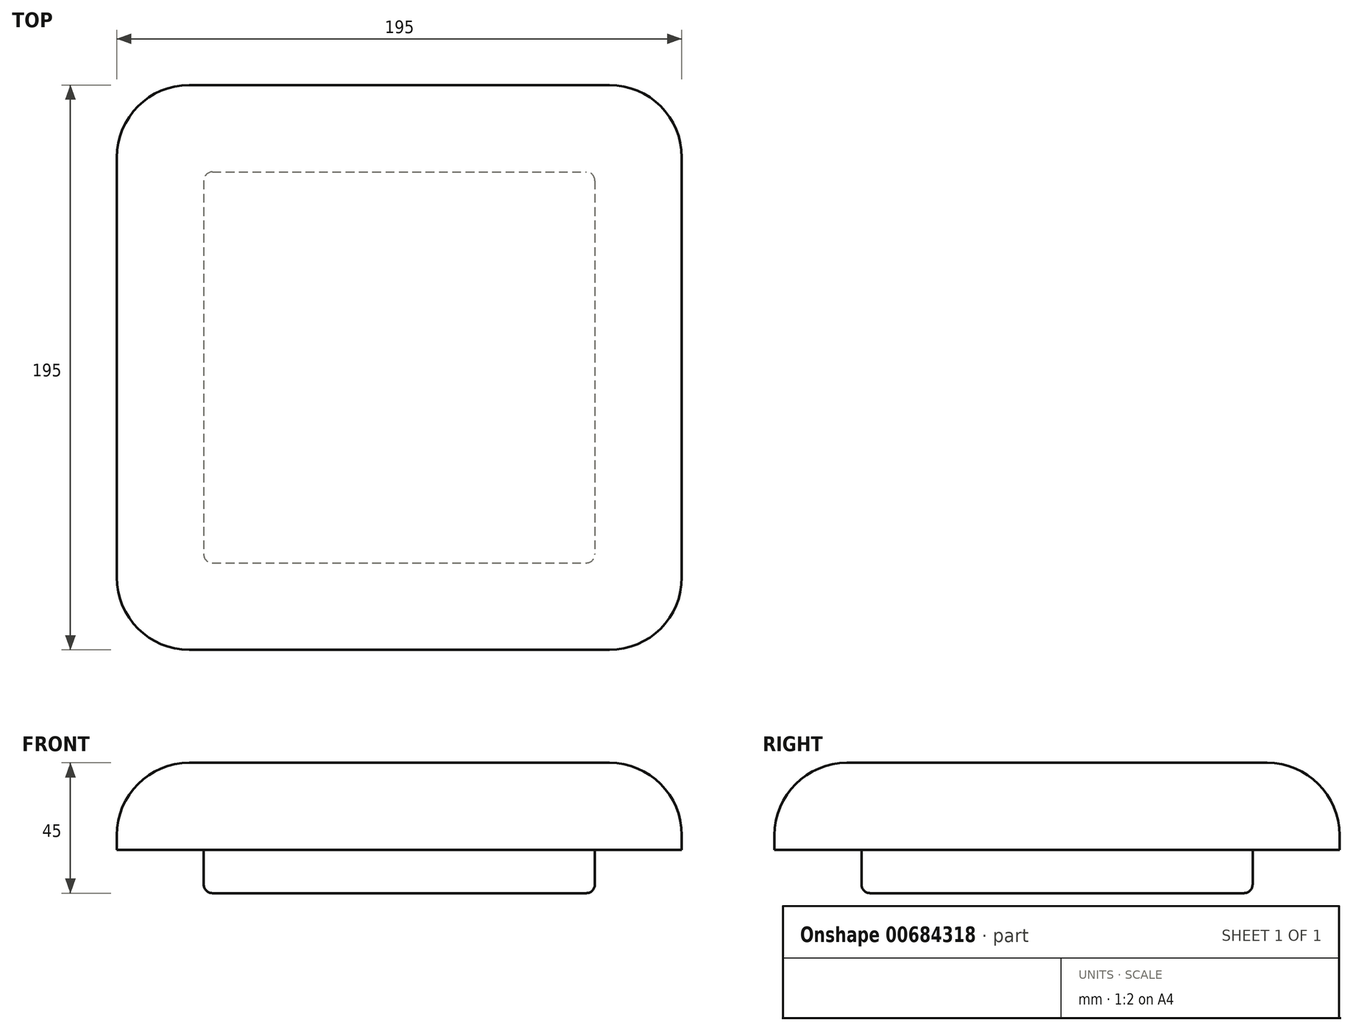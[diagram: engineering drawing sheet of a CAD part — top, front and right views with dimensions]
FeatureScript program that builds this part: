
annotation { "Feature Type Name" : "Feature", "Feature Type Description" : "" }
export const myFeature = defineFeature(function(context is Context, id is Id, definition is map)
    precondition{}
    {
        {
            var Q0;
            Q0=qCreatedBy(makeId("Top.planeOp"),FACE);
            var sketch = newSketch(context, id + "F0", { "sketchPlane" : qUnion([Q0])});
            skLineSegment(sketch, "E0.bottom", {"start": v(97.5, 97.5) * mm, "end": v(-97.5, 97.5) * mm});
            skLineSegment(sketch, "E0.top", {"start": v(97.5, -97.5) * mm, "end": v(-97.5, -97.5) * mm});
            skLineSegment(sketch, "E0.left", {"start": v(97.5, 97.5) * mm, "end": v(97.5, -97.5) * mm});
            skLineSegment(sketch, "E0.right", {"start": v(-97.5, 97.5) * mm, "end": v(-97.5, -97.5) * mm});
            skPoint(sketch, "E0.middle", {"position": v(0, 0) * mm});
            skSolve(sketch);
        }
        {
            var Q0;
            Q0=makeQuery(id+"F0.imprint","IMPRINT",FACE,{"disambiguationData":[TD([[makeQuery(id+"F0.imprint","IMPRINT",EDGE,{"derivedFrom":sQuery(id+"F0.wireOp",EDGE,"E0.bottom")}),1.0]])]});
            extrude(context, id + "F1", {"entities" : qUnion([Q0]), "depth" : 30 * mm, "offsetDistance" : 25 * mm});
        }
        {
            var Q0;
            Q0=makeQuery(id+"F1.opExtrude","CAP_FACE",FACE,{"disambiguationData":[OSD([sQuery(id+"F0.wireOp",EDGE,"E0.bottom"),sQuery(id+"F0.wireOp",EDGE,"E0.top"),sQuery(id+"F0.wireOp",EDGE,"E0.left"),sQuery(id+"F0.wireOp",EDGE,"E0.right")])],"isStart":false});
            var sketch = newSketch(context, id + "F2", { "sketchPlane" : qUnion([Q0])});
            skLineSegment(sketch, "E1.bottom", {"start": v(67.5, 67.5) * mm, "end": v(-67.5, 67.5) * mm});
            skLineSegment(sketch, "E1.top", {"start": v(67.5, -67.5) * mm, "end": v(-67.5, -67.5) * mm});
            skLineSegment(sketch, "E1.left", {"start": v(67.5, 67.5) * mm, "end": v(67.5, -67.5) * mm});
            skLineSegment(sketch, "E1.right", {"start": v(-67.5, 67.5) * mm, "end": v(-67.5, -67.5) * mm});
            skPoint(sketch, "E1.middle", {"position": v(0, 0) * mm});
            skSolve(sketch);
        }
        {
            var Q0;
            Q0=makeQuery(id+"F2.imprint","IMPRINT",FACE,{"disambiguationData":[TD([[makeQuery(id+"F2.imprint","IMPRINT",EDGE,{"derivedFrom":sQuery(id+"F2.wireOp",EDGE,"E1.bottom")}),1.0]])]});
            extrude(context, id + "F3", {"entities" : qUnion([Q0]), "operationType" : NewBodyOperationType.ADD, "depth" : 15 * mm, "offsetDistance" : 25 * mm});
        }
        {
            var Q0;
            Q0=makeQuery(id+"F3.opExtrude","CAP_FACE",FACE,{"disambiguationData":[OSD([sQuery(id+"F2.wireOp",EDGE,"E1.bottom"),sQuery(id+"F2.wireOp",EDGE,"E1.top"),sQuery(id+"F2.wireOp",EDGE,"E1.left"),sQuery(id+"F2.wireOp",EDGE,"E1.right")])],"isStart":false});
            var Q1;
            Q1=makeQuery(id+"F3.opExtrude","SWEPT_EDGE",EDGE,{"disambiguationData":[OSD([sQuery(id+"F2.wireOp",EDGE,"E1.top"),sQuery(id+"F2.wireOp",EDGE,"E1.left")])]});
            var Q2;
            Q2=makeQuery(id+"F3.opExtrude","SWEPT_EDGE",EDGE,{"disambiguationData":[OSD([sQuery(id+"F2.wireOp",EDGE,"E1.bottom"),sQuery(id+"F2.wireOp",EDGE,"E1.left")])]});
            var Q3;
            Q3=makeQuery(id+"F3.opExtrude","SWEPT_EDGE",EDGE,{"disambiguationData":[OSD([sQuery(id+"F2.wireOp",EDGE,"E1.top"),sQuery(id+"F2.wireOp",EDGE,"E1.right")])]});
            var Q4;
            Q4=makeQuery(id+"F3.opExtrude","SWEPT_EDGE",EDGE,{"disambiguationData":[OSD([sQuery(id+"F2.wireOp",EDGE,"E1.bottom"),sQuery(id+"F2.wireOp",EDGE,"E1.right")])]});
            fillet(context, id + "F4", {"entities" : qUnion([Q0, Q1, Q2, Q3, Q4]), "radius" : 3 * mm, "tangentPropagation" : true, "allowEdgeOverflow" : false});
        }
        {
            var Q0;
            Q0=makeQuery(id+"F1.opExtrude","CAP_FACE",FACE,{"disambiguationData":[OSD([sQuery(id+"F0.wireOp",EDGE,"E0.bottom"),sQuery(id+"F0.wireOp",EDGE,"E0.top"),sQuery(id+"F0.wireOp",EDGE,"E0.left"),sQuery(id+"F0.wireOp",EDGE,"E0.right")])],"isStart":true});
            var Q1;
            Q1=makeQuery(id+"F1.opExtrude","SWEPT_EDGE",EDGE,{"disambiguationData":[OSD([sQuery(id+"F0.wireOp",EDGE,"E0.bottom"),sQuery(id+"F0.wireOp",EDGE,"E0.left")])]});
            var Q2;
            Q2=makeQuery(id+"F1.opExtrude","SWEPT_EDGE",EDGE,{"disambiguationData":[OSD([sQuery(id+"F0.wireOp",EDGE,"E0.bottom"),sQuery(id+"F0.wireOp",EDGE,"E0.right")])]});
            var Q3;
            Q3=makeQuery(id+"F1.opExtrude","SWEPT_EDGE",EDGE,{"disambiguationData":[OSD([sQuery(id+"F0.wireOp",EDGE,"E0.top"),sQuery(id+"F0.wireOp",EDGE,"E0.right")])]});
            var Q4;
            Q4=makeQuery(id+"F1.opExtrude","SWEPT_EDGE",EDGE,{"disambiguationData":[OSD([sQuery(id+"F0.wireOp",EDGE,"E0.top"),sQuery(id+"F0.wireOp",EDGE,"E0.left")])]});
            fillet(context, id + "F5", {"entities" : qUnion([Q0, Q1, Q2, Q3, Q4]), "radius" : 25 * mm, "tangentPropagation" : true, "allowEdgeOverflow" : false});
        }
        {
            var Q0;
            Q0=makeQuery(id+"F1.opExtrude","SWEPT_BODY",BODY,{"disambiguationData":[OSD([sQuery(id+"F0.wireOp",EDGE,"E0.bottom"),sQuery(id+"F0.wireOp",EDGE,"E0.top"),sQuery(id+"F0.wireOp",EDGE,"E0.left"),sQuery(id+"F0.wireOp",EDGE,"E0.right")])]});
            var Q1;
            Q1=makeQuery(id+"F1.opExtrude","CAP_EDGE",EDGE,{"disambiguationData":[OSD([sQuery(id+"F0.wireOp",EDGE,"E0.left")])],"isStart":false});
            transform(context, id + "F6", {"entities" : qUnion([Q0]), "transformType" : TransformType.ROTATION, "transformAxis" : qUnion([Q1]), "angle" : 180 * degree, "makeCopy" : false});
        }
        {
            var Q0;
            Q0=makeQuery(id+"F1.opExtrude","SWEPT_BODY",BODY,{"disambiguationData":[OSD([sQuery(id+"F0.wireOp",EDGE,"E0.bottom"),sQuery(id+"F0.wireOp",EDGE,"E0.top"),sQuery(id+"F0.wireOp",EDGE,"E0.left"),sQuery(id+"F0.wireOp",EDGE,"E0.right")])]});
            transform(context, id + "F7", {"entities" : qUnion([Q0]), "transformType" : TransformType.TRANSLATION_3D, "dx" : -195 * mm, "dy" : 0 * mm, "dz" : 0 * mm, "makeCopy" : false});
        }
        {
            var Q0;
            Q0=makeQuery(id+"F1.opExtrude","SWEPT_BODY",BODY,{"disambiguationData":[OSD([sQuery(id+"F0.wireOp",EDGE,"E0.bottom"),sQuery(id+"F0.wireOp",EDGE,"E0.top"),sQuery(id+"F0.wireOp",EDGE,"E0.left"),sQuery(id+"F0.wireOp",EDGE,"E0.right")])]});
            transform(context, id + "F8", {"entities" : qUnion([Q0]), "transformType" : TransformType.TRANSLATION_3D, "dx" : 0 * mm, "dy" : 0 * mm, "dz" : -15 * mm, "makeCopy" : false});
        }
    });
